# Revit family: LED DOWNLIGHT 01_LZ1541WW_CW
name_source: partatom
category: Luminarias
units: mm (PartAtom-declared; Revit-internal decimal feet)

## family parameters
Compartido = No
Corte con vacíos al cargar = No
Cota de conector redondo = Diámetro de uso
Origen de luz = Sí
Punto de cálculo de habitación = No
Se basa en plano de trabajo = Sí
Siempre vertical = Sí
Tipo de pieza = Normal

## types (2) — shared parameters
Cambio de temperatura de color de luz atenuada = <Ninguno>
Elevación por defecto = 1219 mm
Fabricante = BRILLANT
Filtro de color = 16777215
Watt per fixture = 4
Ángulo de campo de foco = 30.00°
Ángulo de enfoque = 30.00°
Ángulo de inclinación = 60.00°

## per-type parameters (varying)
| type | Comentarios de vataje | Descripción | Longitud de símbolo de origen de luz | Lámpara | Modelo |
| DWN_LZ1541WW.30 | 100-240-277V *se requeire accesorio | LUMINARIA TIPO CIRCULAR PARA EMPOTRAR EN TECHO CON CUERPO DE ALUMINIO ACABADO ANONIZADO, IP 20 USO PARA INTERIORES CON CUERPO DE 0.2KG, CUENTA CON 1 LED TIPO CREE CON UNA POTENCIA TOTAL DE 4W, A UNA TEMPERATURA EN BLANCO CALIDO 3000K CON 144LUMENES, EFICIENCIA DE 36LM/W, IRC 80, APERTURA A 30 GRADOS EN STOCK, 700mA EN CORRIENTE DE OPERACIÓN. SE REQUIEREN ACCESORIOS. | 500 mm  [stored 1.64042 ft] | CREE | LZ1541WW.30 |
| DWN_LZ1541CW.30 | 90-240V *se requeire accesorio | LUMINARIA TIPO CIRCULAR PARA EMPOTRAR EN TECHO CON CUERPO DE ALUMINIO ACABADO ANONIZADO, IP 20 USO PARA INTERIORES CON CUERPO DE 0.2KG, CUENTA CON 1 LED TIPO CREE CON UNA POTENCIA TOTAL DE 4W, A UNA TEMPERATURA EN BLANCO FRIO 6000K CON 200LUMENES, EFICIENCIA DE 50LM/W, IRC 80, APERTURA A 30 GRADOS EN STOCK, 700mA EN CORRIENTE DE OPERACIÓN. SE REQUIEREN ACCESORIOS. | 3048 mm  [stored 10 ft] | Cree | LZ1541CW.30 |

note: [stored X ft] marks values corroborated as IEEE doubles in the binary element streams (Revit-internal decimal feet)

## geometry (parser evidence)
native form markers: Blend x2
no freeform markers — native parametric forms only
